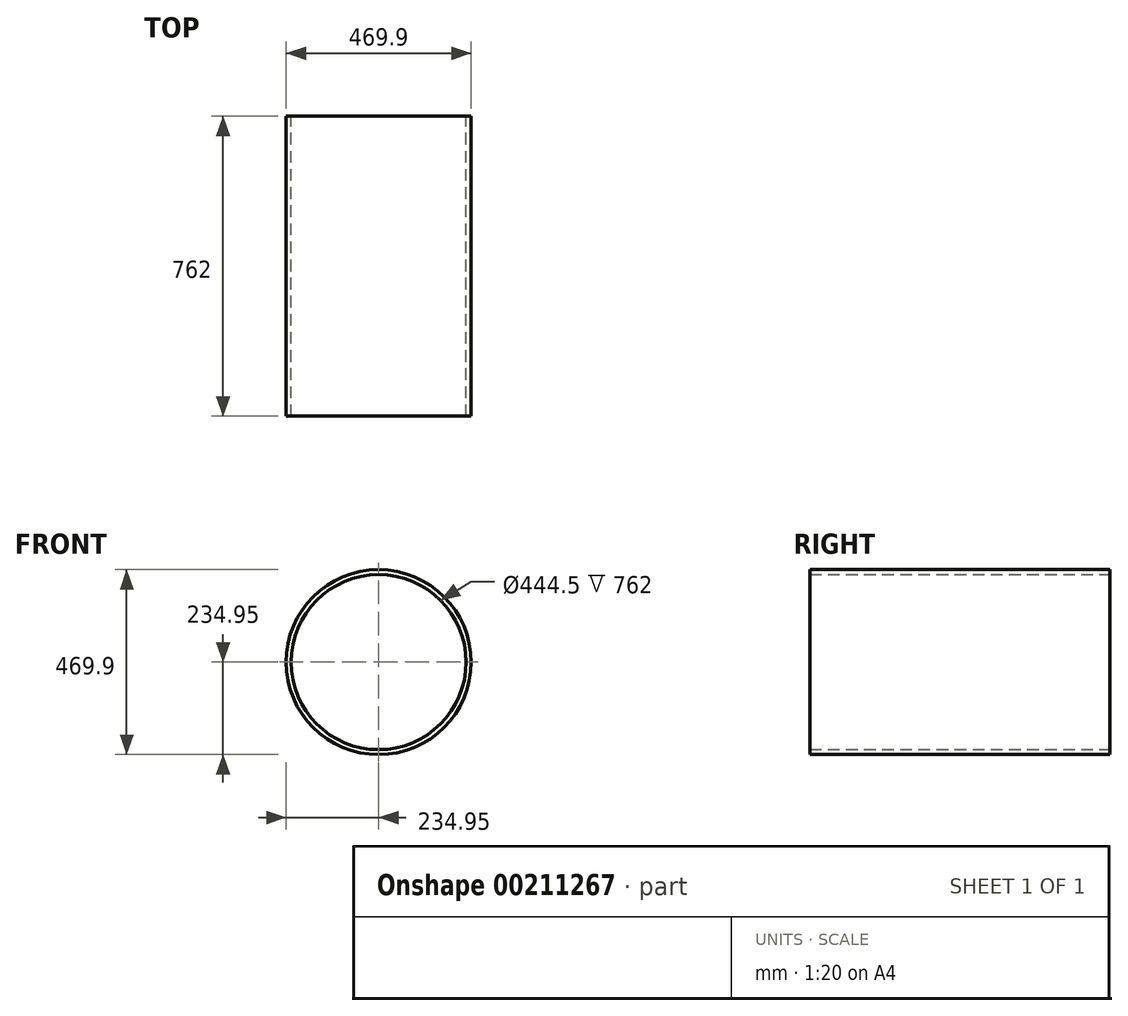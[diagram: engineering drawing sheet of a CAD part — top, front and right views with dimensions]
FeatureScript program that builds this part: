
annotation { "Feature Type Name" : "Feature", "Feature Type Description" : "" }
export const myFeature = defineFeature(function(context is Context, id is Id, definition is map)
    precondition{}
    {
        {
            var Q0;
            Q0=qCreatedBy(makeId("Front.planeOp"),FACE);
            var sketch = newSketch(context, id + "F0", { "sketchPlane" : qUnion([Q0])});
            skCircle(sketch, "E0", {"center": v(0, 0) * mm, "radius": 234.95 * mm});
            skCircle(sketch, "E1", {"center": v(0, 0) * mm, "radius": 222.25 * mm});
            skSolve(sketch);
        }
        {
            var Q0;
            Q0 = qSketchRegion(id + "F0", true);
            extrude(context, id + "F1", {"entities" : qUnion([Q0]), "depth" : 762 * mm});
        }
    });
